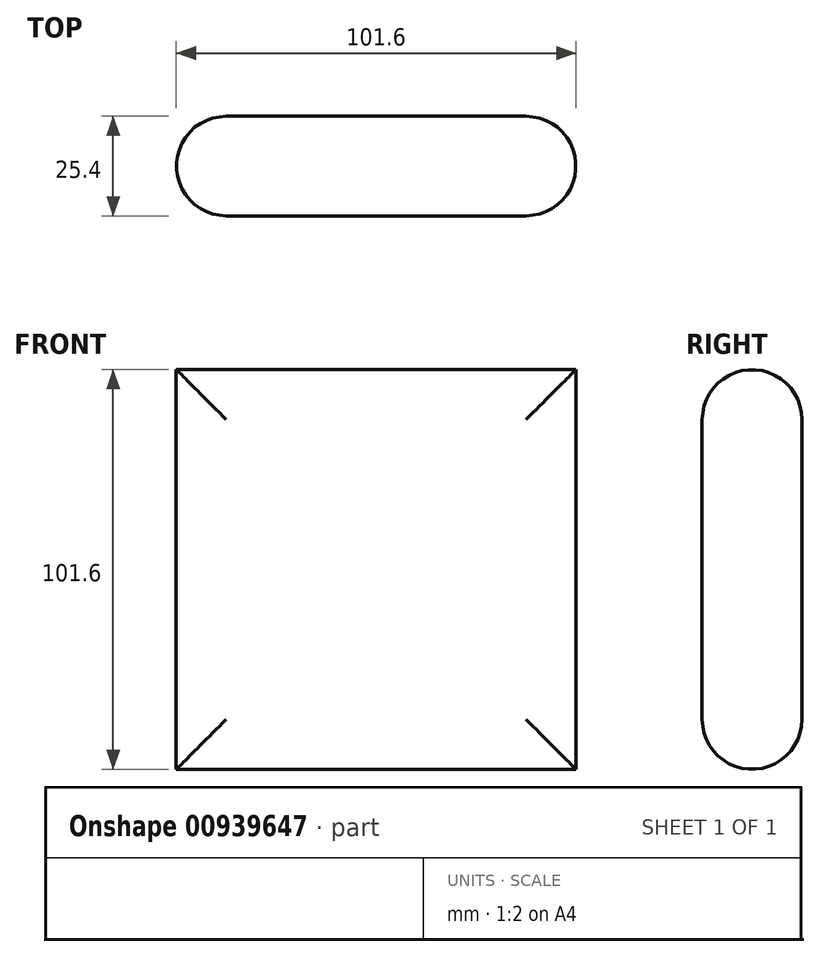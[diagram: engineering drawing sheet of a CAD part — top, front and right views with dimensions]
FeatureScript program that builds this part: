
annotation { "Feature Type Name" : "Feature", "Feature Type Description" : "" }
export const myFeature = defineFeature(function(context is Context, id is Id, definition is map)
    precondition{}
    {
        {
            var Q0;
            Q0=qCreatedBy(makeId("Front.planeOp"),FACE);
            var sketch = newSketch(context, id + "F0", { "sketchPlane" : qUnion([Q0])});
            skLineSegment(sketch, "E0.bottom", {"start": v(-38.25, 36.24) * mm, "end": v(63.35, 36.24) * mm});
            skLineSegment(sketch, "E0.top", {"start": v(-38.25, -65.36) * mm, "end": v(63.35, -65.36) * mm});
            skLineSegment(sketch, "E0.left", {"start": v(-38.25, 36.24) * mm, "end": v(-38.25, -65.36) * mm});
            skLineSegment(sketch, "E0.right", {"start": v(63.35, 36.24) * mm, "end": v(63.35, -65.36) * mm});
            skSolve(sketch);
        }
        {
            var Q0;
            Q0 = qSketchRegion(id + "F0", true);
            extrude(context, id + "F1", {"entities" : qUnion([Q0]), "depth" : 25.4 * mm, "offsetDistance" : 25.4 * mm});
        }
        {
            var Q0;
            Q0=makeQuery(id+"F1.opExtrude","CAP_FACE",FACE,{"disambiguationData":[OSD([sQuery(id+"F0.wireOp",EDGE,"E0.bottom"),sQuery(id+"F0.wireOp",EDGE,"E0.top"),sQuery(id+"F0.wireOp",EDGE,"E0.left"),sQuery(id+"F0.wireOp",EDGE,"E0.right")])],"isStart":true});
            var Q1;
            Q1=makeQuery(id+"F1.opExtrude","CAP_FACE",FACE,{"disambiguationData":[OSD([sQuery(id+"F0.wireOp",EDGE,"E0.bottom"),sQuery(id+"F0.wireOp",EDGE,"E0.top"),sQuery(id+"F0.wireOp",EDGE,"E0.left"),sQuery(id+"F0.wireOp",EDGE,"E0.right")])],"isStart":false});
            fillet(context, id + "F2", {"entities" : qUnion([Q0, Q1]), "radius" : 12.7 * mm, "tangentPropagation" : true, "allowEdgeOverflow" : false});
        }
    });
